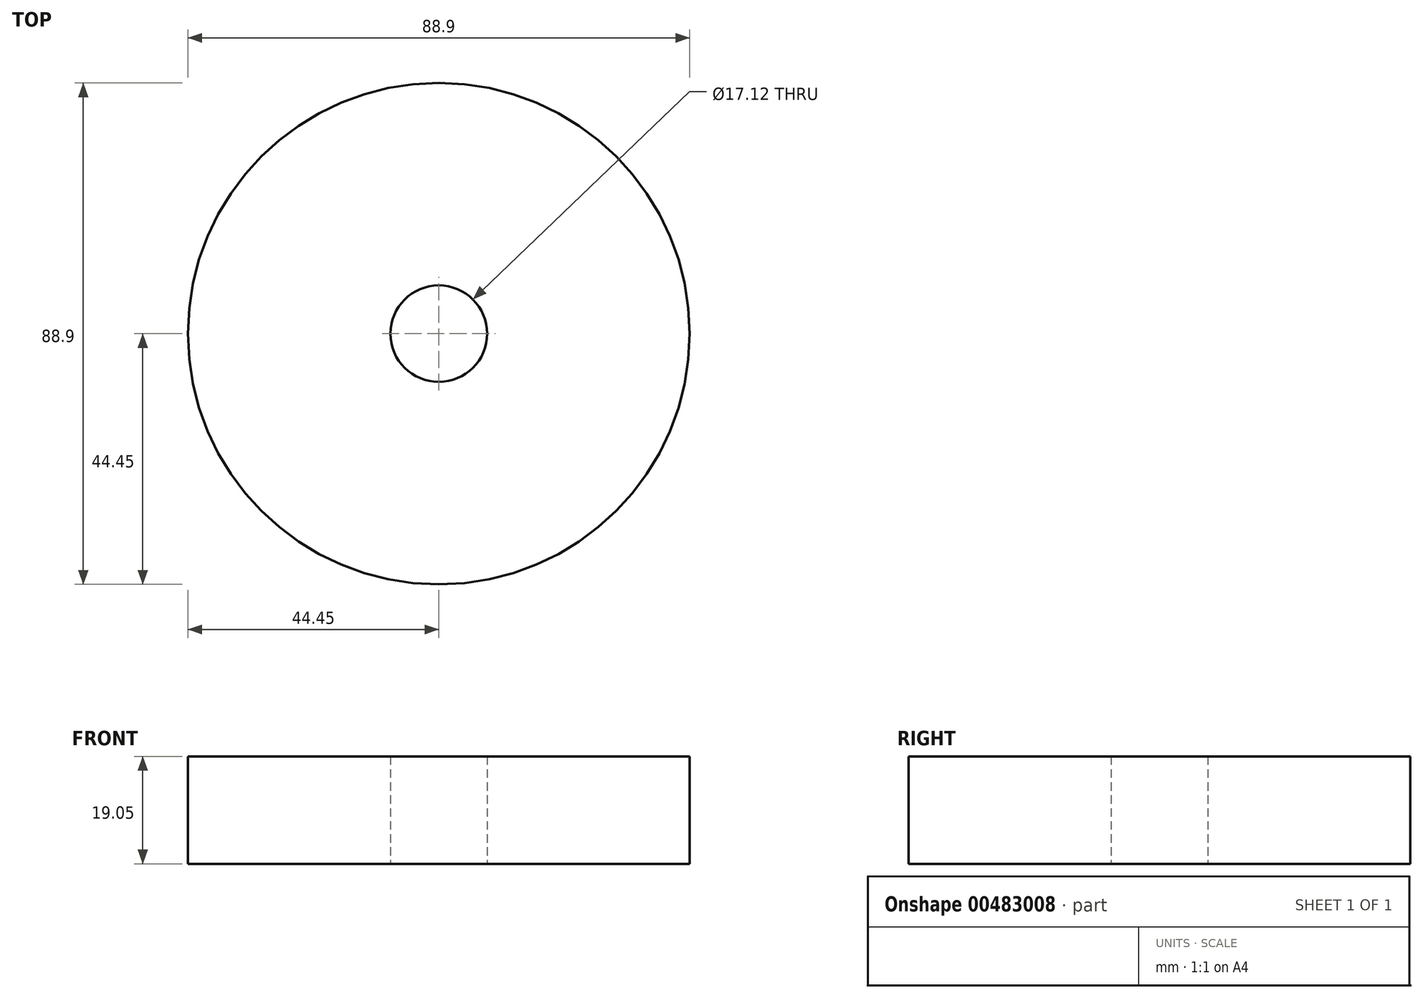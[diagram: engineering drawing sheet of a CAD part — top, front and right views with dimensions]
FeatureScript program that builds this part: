
annotation { "Feature Type Name" : "Feature", "Feature Type Description" : "" }
export const myFeature = defineFeature(function(context is Context, id is Id, definition is map)
    precondition{}
    {
        {
            var Q0;
            Q0=qCreatedBy(makeId("Top.planeOp"),FACE);
            var sketch = newSketch(context, id + "F0", { "sketchPlane" : qUnion([Q0])});
            skCircle(sketch, "E0", {"center": v(0, 0) * mm, "radius": 44.45 * mm});
            skCircle(sketch, "E1", {"center": v(0, 0) * mm, "radius": 8.56 * mm});
            skCircle(sketch, "E2.cCircle", {"center": v(0, 0) * mm, "radius": 15.88 * mm, "construction": true});
            skLineSegment(sketch, "E2.0", {"start": v(15.88, 27.5) * mm, "end": v(15.88, -27.5) * mm, "construction": true});
            skLineSegment(sketch, "E2.1", {"start": v(15.88, -27.5) * mm, "end": v(-31.75, 0) * mm, "construction": true});
            skLineSegment(sketch, "E2.2", {"start": v(-31.75, 0) * mm, "end": v(15.88, 27.5) * mm, "construction": true});
            skPoint(sketch, "E2.0.midPoint", {"position": v(15.88, 0) * mm});
            skSolve(sketch);
        }
        {
            var Q0;
            Q0=makeQuery(id+"F0.imprint","IMPRINT",FACE,{"disambiguationData":[TD([[makeQuery(id+"F0.imprint","IMPRINT",EDGE,{"derivedFrom":sQuery(id+"F0.wireOp",EDGE,"E0")}),1.0]])]});
            extrude(context, id + "F1", {"entities" : qUnion([Q0]), "depth" : 19.05 * mm});
        }
    });
